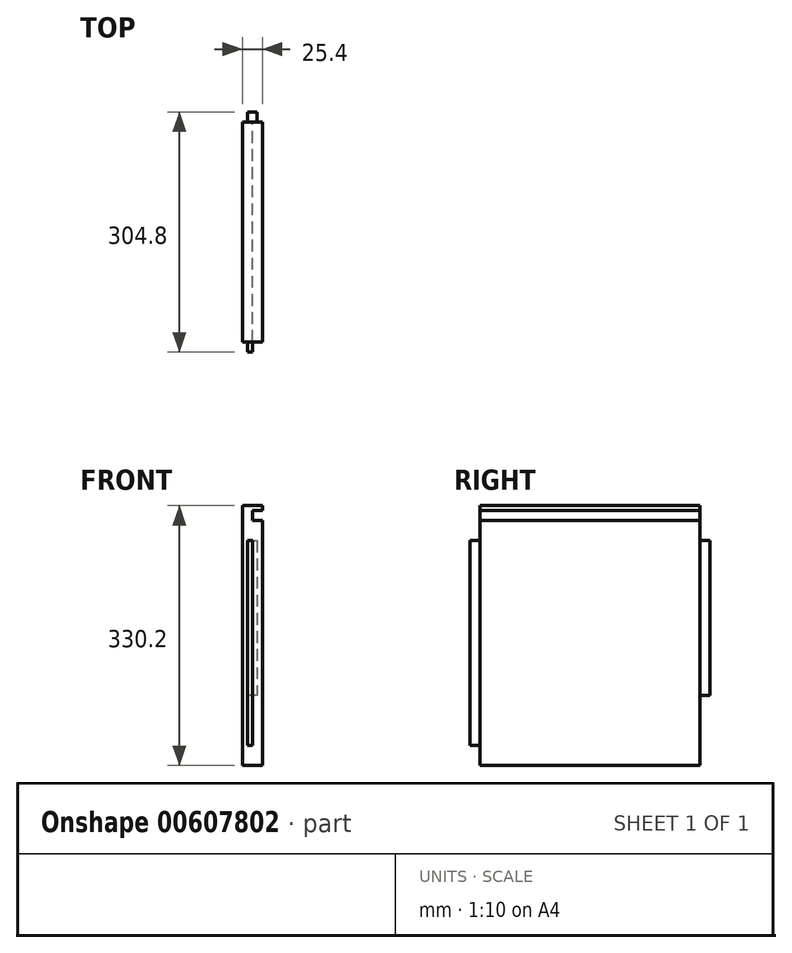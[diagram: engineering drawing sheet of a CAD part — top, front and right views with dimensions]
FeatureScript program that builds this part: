
annotation { "Feature Type Name" : "Feature", "Feature Type Description" : "" }
export const myFeature = defineFeature(function(context is Context, id is Id, definition is map)
    precondition{}
    {
        {
            var Q0;
            Q0=qCreatedBy(makeId("Right.planeOp"),FACE);
            var sketch = newSketch(context, id + "F0", { "sketchPlane" : qUnion([Q0])});
            skLineSegment(sketch, "E0.bottom", {"start": v(0, 0) * mm, "end": v(-279.4, 0) * mm});
            skLineSegment(sketch, "E0.top", {"start": v(0, 304.8) * mm, "end": v(-279.4, 304.8) * mm});
            skLineSegment(sketch, "E0.left", {"start": v(0, 0) * mm, "end": v(0, 304.8) * mm});
            skLineSegment(sketch, "E0.right", {"start": v(-279.4, 0) * mm, "end": v(-279.4, 304.8) * mm});
            skSolve(sketch);
        }
        {
            var Q0;
            Q0=makeQuery(id+"F0.imprint","IMPRINT",FACE,{"disambiguationData":[TD([[makeQuery(id+"F0.imprint","IMPRINT",EDGE,{"derivedFrom":sQuery(id+"F0.wireOp",EDGE,"E0.bottom")}),-1.0]])]});
            extrude(context, id + "F1", {"entities" : qUnion([Q0]), "depth" : 25.4 * mm, "offsetDistance" : 25.4 * mm});
        }
        {
            var Q0;
            Q0=qCreatedBy(makeId("Right.planeOp"),FACE);
            var sketch = newSketch(context, id + "F2", { "sketchPlane" : qUnion([Q0])});
            skLineSegment(sketch, "E1.bottom", {"start": v(0, 0) * mm, "end": v(-279.4, 0) * mm});
            skLineSegment(sketch, "E1.top", {"start": v(0, -25.4) * mm, "end": v(-279.4, -25.4) * mm});
            skLineSegment(sketch, "E1.left", {"start": v(0, 0) * mm, "end": v(0, -25.4) * mm});
            skLineSegment(sketch, "E1.right", {"start": v(-279.4, 0) * mm, "end": v(-279.4, -25.4) * mm});
            skSolve(sketch);
        }
        {
            var Q0;
            Q0=makeQuery(id+"F2.imprint","IMPRINT",FACE,{"disambiguationData":[TD([[makeQuery(id+"F2.imprint","IMPRINT",EDGE,{"derivedFrom":sQuery(id+"F2.wireOp",EDGE,"E1.bottom")}),1.0]])]});
            extrude(context, id + "F3", {"entities" : qUnion([Q0]), "operationType" : NewBodyOperationType.ADD, "depth" : 25.4 * mm, "offsetDistance" : 25.4 * mm});
        }
        {
            var Q0;
            Q0=makeQuery(id+"F3.boolean.opBoolean","MERGE",FACE,{"derivedFrom":[makeQuery(id+"F1.opExtrude","CAP_FACE",FACE,{"disambiguationData":[OSD([sQuery(id+"F0.wireOp",EDGE,"E0.bottom"),sQuery(id+"F0.wireOp",EDGE,"E0.top"),sQuery(id+"F0.wireOp",EDGE,"E0.left"),sQuery(id+"F0.wireOp",EDGE,"E0.right")])],"isStart":false}),makeQuery(id+"F3.opExtrude","CAP_FACE",FACE,{"disambiguationData":[OSD([sQuery(id+"F2.wireOp",EDGE,"E1.bottom"),sQuery(id+"F2.wireOp",EDGE,"E1.top"),sQuery(id+"F2.wireOp",EDGE,"E1.left"),sQuery(id+"F2.wireOp",EDGE,"E1.right")])],"isStart":false})]});
            var sketch = newSketch(context, id + "F4", { "sketchPlane" : qUnion([Q0])});
            skLineSegment(sketch, "E2", {"start": v(-279.4, 304.8) * mm, "end": v(-279.4, 298.45) * mm});
            skLineSegment(sketch, "E3", {"start": v(-279.4, 298.45) * mm, "end": v(-279.4, 285.75) * mm});
            skLineSegment(sketch, "E4", {"start": v(-279.4, 285.75) * mm, "end": v(0, 285.75) * mm});
            skLineSegment(sketch, "E5", {"start": v(0, 285.75) * mm, "end": v(0, 298.45) * mm});
            skLineSegment(sketch, "E6", {"start": v(0, 298.45) * mm, "end": v(-279.4, 298.45) * mm});
            skSolve(sketch);
        }
        {
            var Q0;
            Q0=makeQuery(id+"F4.imprint","IMPRINT",FACE,{"disambiguationData":[TD([[makeQuery(id+"F4.imprint","IMPRINT",EDGE,{"derivedFrom":sQuery(id+"F4.wireOp",EDGE,"E3")}),-1.0]])]});
            extrude(context, id + "F5", {"entities" : qUnion([Q0]), "operationType" : NewBodyOperationType.REMOVE, "oppositeDirection" : true, "depth" : 12.7 * mm, "offsetDistance" : 25.4 * mm});
        }
        {
            var Q0;
            Q0=makeQuery(id+"F3.boolean.opBoolean","MERGE",FACE,{"derivedFrom":[makeQuery(id+"F1.opExtrude","SWEPT_FACE",FACE,{"disambiguationData":[OSD([sQuery(id+"F0.wireOp",EDGE,"E0.right")])]}),makeQuery(id+"F3.opExtrude","SWEPT_FACE",FACE,{"disambiguationData":[OSD([sQuery(id+"F2.wireOp",EDGE,"E1.right")])]})]});
            var sketch = newSketch(context, id + "F6", { "sketchPlane" : qUnion([Q0])});
            skLineSegment(sketch, "E7", {"start": v(0, 304.8) * mm, "end": v(0, 260.35) * mm});
            skLineSegment(sketch, "E8", {"start": v(0, 260.35) * mm, "end": v(6.35, 260.35) * mm});
            skLineSegment(sketch, "E9", {"start": v(6.35, 260.35) * mm, "end": v(6.35, 0) * mm});
            skLineSegment(sketch, "E10", {"start": v(6.35, 0) * mm, "end": v(12.7, 0) * mm});
            skLineSegment(sketch, "E11", {"start": v(12.7, 0) * mm, "end": v(12.7, 260.35) * mm});
            skLineSegment(sketch, "E12", {"start": v(12.7, 260.35) * mm, "end": v(6.35, 260.35) * mm});
            skSolve(sketch);
        }
        {
            var Q0;
            Q0=makeQuery(id+"F6.imprint","IMPRINT",FACE,{"disambiguationData":[TD([[makeQuery(id+"F6.imprint","IMPRINT",EDGE,{"derivedFrom":sQuery(id+"F6.wireOp",EDGE,"E9")}),1.0]])]});
            extrude(context, id + "F7", {"entities" : qUnion([Q0]), "operationType" : NewBodyOperationType.ADD, "depth" : 12.7 * mm, "offsetDistance" : 25.4 * mm});
        }
        {
            var Q0;
            Q0=makeQuery(id+"F3.boolean.opBoolean","MERGE",FACE,{"derivedFrom":[makeQuery(id+"F1.opExtrude","SWEPT_FACE",FACE,{"disambiguationData":[OSD([sQuery(id+"F0.wireOp",EDGE,"E0.left")])]}),makeQuery(id+"F3.opExtrude","SWEPT_FACE",FACE,{"disambiguationData":[OSD([sQuery(id+"F2.wireOp",EDGE,"E1.left")])]})]});
            var sketch = newSketch(context, id + "F8", { "sketchPlane" : qUnion([Q0])});
            skLineSegment(sketch, "E13", {"start": v(0, 304.8) * mm, "end": v(0, 260.35) * mm});
            skLineSegment(sketch, "E14", {"start": v(0, 260.35) * mm, "end": v(-6.35, 260.35) * mm});
            skLineSegment(sketch, "E15", {"start": v(-6.35, 260.35) * mm, "end": v(-19.05, 260.35) * mm});
            skLineSegment(sketch, "E16", {"start": v(-19.05, 260.35) * mm, "end": v(-19.05, 63.5) * mm});
            skLineSegment(sketch, "E17", {"start": v(-19.05, 63.5) * mm, "end": v(-6.35, 63.5) * mm});
            skLineSegment(sketch, "E18", {"start": v(-6.35, 63.5) * mm, "end": v(-6.35, 260.35) * mm});
            skSolve(sketch);
        }
        {
            var Q0;
            Q0=makeQuery(id+"F8.imprint","IMPRINT",FACE,{"disambiguationData":[TD([[makeQuery(id+"F8.imprint","IMPRINT",EDGE,{"derivedFrom":sQuery(id+"F8.wireOp",EDGE,"E15")}),1.0]])]});
            extrude(context, id + "F9", {"entities" : qUnion([Q0]), "operationType" : NewBodyOperationType.ADD, "depth" : 12.7 * mm, "offsetDistance" : 25.4 * mm});
        }
    });
